# Revit family: G-2015_Valvula_Valvulas-Arco_Tajo-Pro
name_source: partatom
category: Pipe Accessories
revit_build: Autodesk Revit 2015 (Build: 20140223_1515(x64)
units: mm (PartAtom-declared; Revit-internal decimal feet)

## types (3) — shared parameters
Acabado = Cromado
Autor = Bimetica PDS
COBieCategoria = IfcValve
Clase Brida = PN16
ClasificacionDeCierre = 0.00 bar
CodigoGubimclass = 50.10.20.10
CoeficienteDeCaudal = 418
DescripcionGubimclass = Válvulas e instrumentos de medida y control de flujo de fontanería
Description = Válvula esfera doble eje TAJO PRO doble mando conexión embridada
Diam. Agujeros = 18.000 mm
F = 30.000 mm
FechaEmisionElementoBIM = 11/02/2020
FechaVencimientoElementoBIM = 11/02/2021
GarantiaExtendida = Yes
Historial = (RVT2015-V01) Creación del elemento
IfcExportAs = IfcValve
IfcExportType = Ball Valve
K Coefficient = 0.35
Manufacturer = Vávulas Arco S.L
Marcado CE = Yes
MasterformatCodigo = 35 20 19
MasterformatTitulo = Hydraulic Valves
MaterialCarcasa = Latón Europeo CW617N
MecanismoValvula = BALL
Model = TAJO PRO BRIDAS
No. Agujeros = 8
Numero de Licencia = XXX-XXXX9536
OmniclassCodigo = 23-27 31 15
OmniclassTitulo = Ball Valves
OperacionValvula = PALANCA
PatronValvula = STRAIGHT_2_PORT
PresionDePrueba = 0.00 bar
PresionDeTrabajo = 0.00 bar
PresionNominal = 30.00 bar
Radio Agujero = 9.000 mm
Sistema = Agua potable y agua caliente sanitaria
TelefonoContacto = 0034 963 17 10 70
TemperaturaMaxima = 140 °C
TemprerturaMinima = -20 °C
Titular = Vávulas Arco S.L
Type Comments = Agua potable y agua caliente sanitaria
UNSPSCCodigo = 40141607
UNSPSCTitulo = Ball valves
URLPerfilProductoBimetica = https://bimetica.com
Uniclass2015Codigo = 65-54-95-13
Uniclass2015Titulo = Check valves
Version = RVT2015
zero-valued in all types: AcidificacionAtmosfericaPorUnidad, AguaConsumidaPorUnidad, CambioClimaticoPorUnidad, CosteMantenimiento, CurvaSonido, DestruccionCapaOzonoEstratosfericaPorUnidad, Energia consumida, EnergiaNoRenovableConsumidaPorUnidad, EnergiaPrimariaTotalConsumidaPorUnidad, EnergiaRenovableConsumidaPorUnidad, EutrofizacionPorUnidad, FaltaDeRecursosPorUnidad, FechaEvaluacion, FormacionFotoquimicaOzonoPorUnidad, ResiduoInertePorUnidad, ResiduoRadioactivoPorUnidad, ResiduosNoPeligrososPorUnidad, ResiduosPeligrososPorUnidad

## per-type parameters (varying)
| type | A | A di | B | C - Longitud | Codigo | Cost | D | E | R | Radio A di | Radio D | Radio Nominal | Referencia | Tamano |
| 2H x 2H | 154.000 mm | 129.000 mm | 203.000 mm | 126.000 mm | 01036AC | 80.68€ | 50.800 mm | 96.000 mm | 1" | 64.500 mm | 30.480 mm | 31.750 mm | 01036AC | 2" |
| 2½H x 2½H | 174.000 mm | 149.000 mm | 223.000 mm | 150.000 mm | 01036AC | 124.17€ | 63.500 mm | 116.000 mm | 1" | 74.500 mm | 38.100 mm | 25.400 mm | 01036AC | 3" |
| 3H x 3H | 215.000 mm | 190.000 mm | 298.000 mm | 164.000 mm | 01038AC | 272.43€ | 76.200 mm | 103.000 mm | 2" | 95.000 mm | 45.720 mm | 38.100 mm | 01038AC | 3" |

## geometry (parser evidence)
native form markers: Sweep x1
no freeform markers — native parametric forms only
